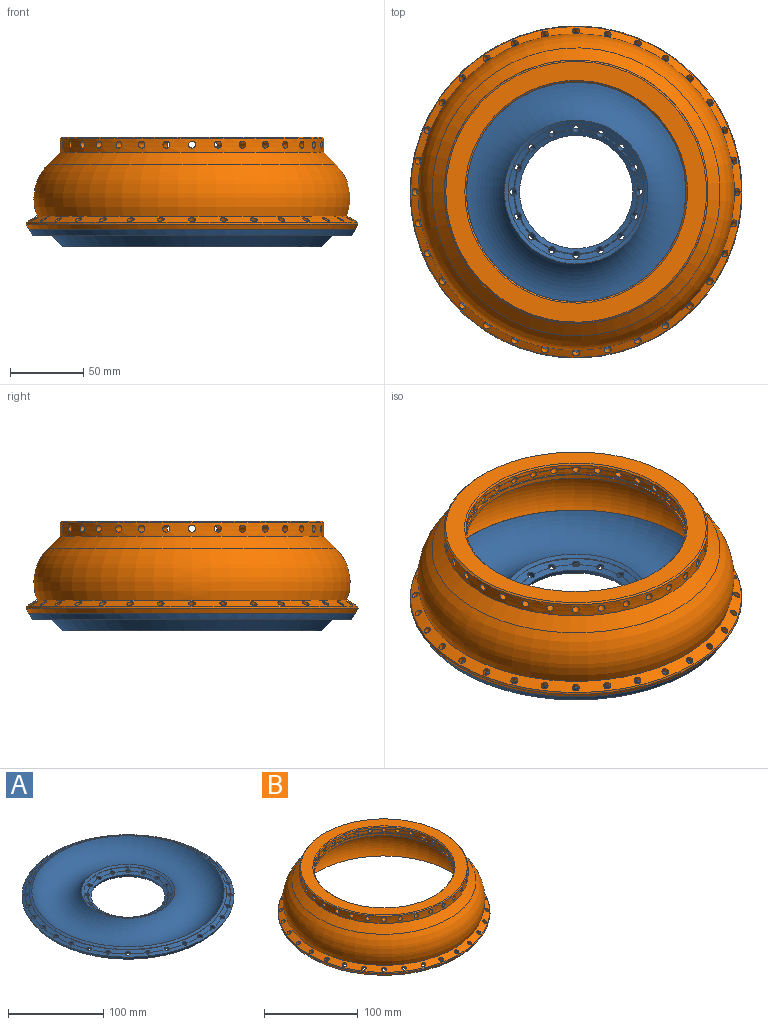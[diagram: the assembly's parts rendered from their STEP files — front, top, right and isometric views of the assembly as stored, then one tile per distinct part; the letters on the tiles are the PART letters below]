
ASSEMBLY  parts=2 mates=1
PART A: 112 faces, bbox 227.3x227.3x33 mm
  f0: cone r=42.59mm half-angle=30deg, axis (0,0,-1), area 12.1mm2, adj f1,f59,f65,f111
  f1: cone r=46.92mm half-angle=60deg, axis (0,0,1), area 1208mm2, adj f0,f2,f3,f4,f5,f6,f7,f8
  f2: cone r=42.59mm half-angle=30deg, axis (0,0,-1), area 12.1mm2, adj f1,f59,f110,f111
  f3: cone r=42.59mm half-angle=30deg, axis (0,0,-1), area 12.1mm2, adj f1,f59,f109,f110
  f4: cone r=42.59mm half-angle=30deg, axis (0,0,-1), area 12.1mm2, adj f1,f59,f108,f109
  f5: cone r=42.59mm half-angle=30deg, axis (0,0,-1), area 12.1mm2, adj f1,f59,f107,f108
  f6: cone r=42.59mm half-angle=30deg, axis (0,0,-1), area 12.1mm2, adj f1,f59,f106,f107
  f7: cone r=42.59mm half-angle=30deg, axis (0,0,-1), area 12.1mm2, adj f1,f59,f105,f106
  f8: cone r=42.59mm half-angle=30deg, axis (0,0,-1), area 12.1mm2, adj f1,f59,f104,f105
  f9: cone r=42.59mm half-angle=30deg, axis (0,0,-1), area 12.1mm2, adj f1,f59,f103,f104
  f10: cone r=42.59mm half-angle=30deg, axis (0,0,-1), area 12.1mm2, adj f1,f59,f102,f103
  f11: cone r=42.59mm half-angle=30deg, axis (0,0,-1), area 12.1mm2, adj f1,f59,f101,f102
  f12: cone r=42.59mm half-angle=30deg, axis (0,0,-1), area 12.1mm2, adj f1,f59,f100,f101
  f13: cone r=42.59mm half-angle=30deg, axis (0,0,-1), area 12.1mm2, adj f1,f59,f99,f100
  f14: cone r=42.59mm half-angle=30deg, axis (0,0,-1), area 12.1mm2, adj f1,f59,f98,f99
  f15: cone r=42.59mm half-angle=30deg, axis (0,0,-1), area 12.1mm2, adj f1,f59,f97,f98
  f16: cone r=107.41mm half-angle=30deg, axis (0,0,1), area 16.5mm2, adj f49,f51,f64,f96
  f17: cone r=107.41mm half-angle=30deg, axis (0,0,1), area 16.5mm2, adj f49,f51,f95,f96
  f18: cone r=107.41mm half-angle=30deg, axis (0,0,1), area 16.5mm2, adj f49,f51,f94,f95
  f19: cone r=107.41mm half-angle=30deg, axis (0,0,1), area 16.5mm2, adj f49,f51,f93,f94
  f20: cone r=107.41mm half-angle=30deg, axis (0,0,1), area 16.5mm2, adj f49,f51,f92,f93
  f21: cone r=107.41mm half-angle=30deg, axis (0,0,1), area 16.5mm2, adj f49,f51,f91,f92
  f22: cone r=107.41mm half-angle=30deg, axis (0,0,1), area 16.5mm2, adj f49,f51,f90,f91
  f23: cone r=107.41mm half-angle=30deg, axis (0,0,1), area 16.5mm2, adj f49,f51,f89,f90
  f24: cone r=107.41mm half-angle=30deg, axis (0,0,1), area 16.5mm2, adj f49,f51,f88,f89
  f25: cone r=107.41mm half-angle=30deg, axis (0,0,1), area 16.5mm2, adj f49,f51,f87,f88
  f26: cone r=107.41mm half-angle=30deg, axis (0,0,1), area 16.5mm2, adj f49,f51,f86,f87
  f27: cone r=107.41mm half-angle=30deg, axis (0,0,1), area 16.5mm2, adj f49,f51,f85,f86
  f28: cone r=107.41mm half-angle=30deg, axis (0,0,1), area 16.5mm2, adj f49,f51,f84,f85
  f29: cone r=107.41mm half-angle=30deg, axis (0,0,1), area 16.5mm2, adj f49,f51,f83,f84
  f30: cone r=107.41mm half-angle=30deg, axis (0,0,1), area 16.5mm2, adj f49,f51,f82,f83
  f31: cone r=107.41mm half-angle=30deg, axis (0,0,1), area 16.5mm2, adj f49,f51,f81,f82
  f32: cone r=107.41mm half-angle=30deg, axis (0,0,1), area 16.5mm2, adj f49,f51,f80,f81
  f33: cone r=107.41mm half-angle=30deg, axis (0,0,1), area 16.5mm2, adj f49,f51,f79,f80
  f34: cone r=107.41mm half-angle=30deg, axis (0,0,1), area 16.5mm2, adj f49,f51,f78,f79
  f35: cone r=107.41mm half-angle=30deg, axis (0,0,1), area 16.5mm2, adj f49,f51,f77,f78
  f36: cone r=107.41mm half-angle=30deg, axis (0,0,1), area 16.5mm2, adj f49,f51,f76,f77
  f37: cone r=107.41mm half-angle=30deg, axis (0,0,1), area 16.5mm2, adj f49,f51,f75,f76
  f38: cone r=107.41mm half-angle=30deg, axis (0,0,1), area 16.5mm2, adj f49,f51,f74,f75
  f39: cone r=107.41mm half-angle=30deg, axis (0,0,1), area 16.5mm2, adj f49,f51,f73,f74
  f40: cone r=107.41mm half-angle=30deg, axis (0,0,1), area 16.5mm2, adj f49,f51,f72,f73
  f41: cone r=107.41mm half-angle=30deg, axis (0,0,1), area 16.5mm2, adj f49,f51,f71,f72
  f42: cone r=107.41mm half-angle=30deg, axis (0,0,1), area 16.5mm2, adj f49,f51,f70,f71
  f43: cone r=107.41mm half-angle=30deg, axis (0,0,1), area 16.5mm2, adj f49,f51,f69,f70
  f44: cone r=107.41mm half-angle=30deg, axis (0,0,1), area 16.5mm2, adj f49,f51,f68,f69
  f45: cone r=107.41mm half-angle=30deg, axis (0,0,1), area 16.5mm2, adj f49,f51,f67,f68
  f46: cone r=107.41mm half-angle=30deg, axis (0,0,1), area 16.5mm2, adj f49,f51,f66,f67
  f47: cone r=100.98mm half-angle=60deg, axis (0,0,-1), area 1927.9mm2, adj f48,f63
  f48: cone r=103.58mm half-angle=30deg, axis (0,0,1), area 649.2mm2, adj f47,f49
  f49: cone r=103.08mm half-angle=60deg, axis (0,0,-1), area 2913.7mm2, adj f16,f17,f18,f19,f20,f21,f22,f23
  f50: cone r=107.41mm half-angle=30deg, axis (0,0,1), area 16.5mm2, adj f49,f51,f64,f66
  f51: cone r=107.91mm half-angle=60deg, axis (0,0,-1), area 2569.7mm2, adj f16,f17,f18,f19,f20,f21,f22,f23
  f52: cone r=111.37mm half-angle=30deg, axis (0,0,1), area 3459.6mm2, adj f51,f53
  f53: cone r=108.87mm half-angle=60deg, axis (0,0,-1), area 5598.7mm2, adj f52,f54,f64,f66,f67,f68,f69,f70
  f54: cone r=100.75mm half-angle=45deg, axis (0,0,1), area 10386.6mm2, adj f53,f55
  f55: plane 176.78x176.78mm, normal (0,0,-1), area 12618.4mm2, adj f54,f56
  f56: cone r=49.25mm half-angle=45deg, axis (0,0,-1), area 6088.1mm2, adj f55,f57
  f57: cone r=41.13mm half-angle=60deg, axis (0,0,1), area 2373.1mm2, adj f56,f58,f65,f97,f98,f99,f100,f101
  f58: cone r=38.63mm half-angle=30deg, axis (0,0,-1), area 1252.8mm2, adj f57,f59
  f59: cone r=42.09mm half-angle=60deg, axis (0,0,1), area 923.1mm2, adj f0,f2,f3,f4,f5,f6,f7,f8
  f60: cone r=42.59mm half-angle=30deg, axis (0,0,-1), area 12.1mm2, adj f1,f59,f65,f97
  f61: cone r=46.42mm half-angle=30deg, axis (0,0,-1), area 293.2mm2, adj f1,f62
  f62: cone r=49.02mm half-angle=60deg, axis (0,0,1), area 899.5mm2, adj f61,f63
  f63: torus R=75mm, axis (0,0,1), area 29608.8mm2, adj f47,f62
  f64: cylinder r=2.4mm len=6.73mm, axis (0.5,0,-0.87), area 66.4mm2, adj f16,f49,f50,f51,f53
  f65: cylinder r=2.4mm len=6.76mm, axis (-0.5,0,-0.87), area 66.4mm2, adj f0,f1,f57,f59,f60
  f66: cylinder r=2.4mm len=6.73mm, axis (0.49,0.1,-0.87), area 66.4mm2, adj f46,f49,f50,f51,f53
  f67: cylinder r=2.4mm len=6.73mm, axis (0.46,0.19,-0.87), area 66.4mm2, adj f45,f46,f49,f51,f53
  f68: cylinder r=2.4mm len=6.73mm, axis (0.42,0.28,-0.87), area 66.4mm2, adj f44,f45,f49,f51,f53
  f69: cylinder r=2.4mm len=6.73mm, axis (0.35,0.35,-0.87), area 66.4mm2, adj f43,f44,f49,f51,f53
  f70: cylinder r=2.4mm len=6.73mm, axis (0.28,0.42,-0.87), area 66.4mm2, adj f42,f43,f49,f51,f53
  f71: cylinder r=2.4mm len=6.73mm, axis (0.19,0.46,-0.87), area 66.4mm2, adj f41,f42,f49,f51,f53
  f72: cylinder r=2.4mm len=6.73mm, axis (0.1,0.49,-0.87), area 66.5mm2, adj f40,f41,f49,f51,f53
  f73: cylinder r=2.4mm len=6.73mm, axis (0,0.5,-0.87), area 66.4mm2, adj f39,f40,f49,f51,f53
  f74: cylinder r=2.4mm len=6.73mm, axis (-0.1,0.49,-0.87), area 66.5mm2, adj f38,f39,f49,f51,f53
  f75: cylinder r=2.4mm len=6.73mm, axis (-0.19,0.46,-0.87), area 66.5mm2, adj f37,f38,f49,f51,f53
  f76: cylinder r=2.4mm len=6.73mm, axis (-0.28,0.42,-0.87), area 66.5mm2, adj f36,f37,f49,f51,f53
  f77: cylinder r=2.4mm len=6.73mm, axis (-0.35,0.35,-0.87), area 66.5mm2, adj f35,f36,f49,f51,f53
  f78: cylinder r=2.4mm len=6.73mm, axis (-0.42,0.28,-0.87), area 66.5mm2, adj f34,f35,f49,f51,f53
  f79: cylinder r=2.4mm len=6.73mm, axis (-0.46,0.19,-0.87), area 66.5mm2, adj f33,f34,f49,f51,f53
  f80: cylinder r=2.4mm len=6.73mm, axis (-0.49,0.1,-0.87), area 66.5mm2, adj f32,f33,f49,f51,f53
  f81: cylinder r=2.4mm len=6.72mm, axis (-0.5,0,-0.87), area 66.4mm2, adj f31,f32,f49,f51,f53
  f82: cylinder r=2.4mm len=6.72mm, axis (-0.49,-0.1,-0.87), area 66.4mm2, adj f30,f31,f49,f51,f53
  f83: cylinder r=2.4mm len=6.72mm, axis (-0.46,-0.19,-0.87), area 66.4mm2, adj f29,f30,f49,f51,f53
  f84: cylinder r=2.4mm len=6.72mm, axis (-0.42,-0.28,-0.87), area 66.4mm2, adj f28,f29,f49,f51,f53
  f85: cylinder r=2.4mm len=6.73mm, axis (-0.35,-0.35,-0.87), area 66.4mm2, adj f27,f28,f49,f51,f53
  f86: cylinder r=2.4mm len=6.73mm, axis (-0.28,-0.42,-0.87), area 66.4mm2, adj f26,f27,f49,f51,f53
  f87: cylinder r=2.4mm len=6.73mm, axis (-0.19,-0.46,-0.87), area 66.4mm2, adj f25,f26,f49,f51,f53
  f88: cylinder r=2.4mm len=6.73mm, axis (-0.1,-0.49,-0.87), area 66.5mm2, adj f24,f25,f49,f51,f53
  f89: cylinder r=2.4mm len=6.73mm, axis (0,-0.5,-0.87), area 66.4mm2, adj f23,f24,f49,f51,f53
  f90: cylinder r=2.4mm len=6.73mm, axis (0.1,-0.49,-0.87), area 66.5mm2, adj f22,f23,f49,f51,f53
  f91: cylinder r=2.4mm len=6.73mm, axis (0.19,-0.46,-0.87), area 66.5mm2, adj f21,f22,f49,f51,f53
  f92: cylinder r=2.4mm len=6.73mm, axis (0.28,-0.42,-0.87), area 66.5mm2, adj f20,f21,f49,f51,f53
  f93: cylinder r=2.4mm len=6.73mm, axis (0.35,-0.35,-0.87), area 66.5mm2, adj f19,f20,f49,f51,f53
  f94: cylinder r=2.4mm len=6.73mm, axis (0.42,-0.28,-0.87), area 66.4mm2, adj f18,f19,f49,f51,f53
  f95: cylinder r=2.4mm len=6.73mm, axis (0.46,-0.19,-0.87), area 66.4mm2, adj f17,f18,f49,f51,f53
  f96: cylinder r=2.4mm len=6.73mm, axis (0.49,-0.1,-0.87), area 66.5mm2, adj f16,f17,f49,f51,f53
  f97: cylinder r=2.4mm len=6.76mm, axis (-0.46,-0.19,-0.87), area 66.4mm2, adj f1,f15,f57,f59,f60
  f98: cylinder r=2.4mm len=6.76mm, axis (-0.35,-0.35,-0.87), area 66.3mm2, adj f1,f14,f15,f57,f59
  f99: cylinder r=2.4mm len=6.76mm, axis (-0.19,-0.46,-0.87), area 66.4mm2, adj f1,f13,f14,f57,f59
  f100: cylinder r=2.4mm len=6.76mm, axis (0,-0.5,-0.87), area 66.4mm2, adj f1,f12,f13,f57,f59
  f101: cylinder r=2.4mm len=6.76mm, axis (0.19,-0.46,-0.87), area 66.4mm2, adj f1,f11,f12,f57,f59
  f102: cylinder r=2.4mm len=6.76mm, axis (0.35,-0.35,-0.87), area 66.4mm2, adj f1,f10,f11,f57,f59
  f103: cylinder r=2.4mm len=6.76mm, axis (0.46,-0.19,-0.87), area 66.4mm2, adj f1,f9,f10,f57,f59
  f104: cylinder r=2.4mm len=6.76mm, axis (0.5,0,-0.87), area 66.3mm2, adj f1,f8,f9,f57,f59
  f105: cylinder r=2.4mm len=6.76mm, axis (0.46,0.19,-0.87), area 66.4mm2, adj f1,f7,f8,f57,f59
  f106: cylinder r=2.4mm len=6.76mm, axis (0.35,0.35,-0.87), area 66.4mm2, adj f1,f6,f7,f57,f59
  f107: cylinder r=2.4mm len=6.76mm, axis (0.19,0.46,-0.87), area 66.4mm2, adj f1,f5,f6,f57,f59
  f108: cylinder r=2.4mm len=6.76mm, axis (0,0.5,-0.87), area 66.4mm2, adj f1,f4,f5,f57,f59
  f109: cylinder r=2.4mm len=6.76mm, axis (-0.19,0.46,-0.87), area 66.4mm2, adj f1,f3,f4,f57,f59
  f110: cylinder r=2.4mm len=6.76mm, axis (-0.35,0.35,-0.87), area 66.4mm2, adj f1,f2,f3,f57,f59
  f111: cylinder r=2.4mm len=6.76mm, axis (-0.46,0.19,-0.87), area 66.3mm2, adj f0,f1,f2,f57,f59
PART B: 157 faces, bbox 233.8x233.8x65.4 mm
  f0: cone r=108.41mm half-angle=30deg, axis (0,0,1), area 16.6mm2, adj f73,f75,f80,f153
  f1: plane 10.45x4.04mm, normal (0,0,-1), area 10.6mm2, adj f64,f66,f150,f152
  f2: cone r=108.41mm half-angle=30deg, axis (0,0,1), area 16.6mm2, adj f73,f75,f149,f151
  f3: plane 9.83x5.88mm, normal (0,0,-1), area 10.6mm2, adj f64,f66,f148,f150
  f4: cone r=108.41mm half-angle=30deg, axis (0,0,1), area 16.6mm2, adj f73,f75,f151,f153
  f5: plane 8.84x7.51mm, normal (0,0,-1), area 10.6mm2, adj f64,f66,f146,f148
  f6: cone r=108.41mm half-angle=30deg, axis (0,0,1), area 16.6mm2, adj f73,f75,f147,f149
  f7: plane 8.84x7.51mm, normal (0,0,-1), area 10.6mm2, adj f64,f66,f144,f146
  f8: cone r=108.41mm half-angle=30deg, axis (0,0,1), area 16.6mm2, adj f73,f75,f145,f147
  f9: plane 9.83x5.88mm, normal (0,0,-1), area 10.6mm2, adj f64,f66,f142,f144
  f10: cone r=108.41mm half-angle=30deg, axis (0,0,1), area 16.6mm2, adj f73,f75,f143,f145
  f11: plane 10.45x4.04mm, normal (0,0,-1), area 10.6mm2, adj f64,f66,f140,f142
  f12: cone r=108.41mm half-angle=30deg, axis (0,0,1), area 16.6mm2, adj f73,f75,f141,f143
  f13: plane 10.67x2.03mm, normal (0,0,-1), area 10.6mm2, adj f64,f66,f138,f140
  f14: cone r=108.41mm half-angle=30deg, axis (0,0,1), area 16.6mm2, adj f73,f75,f139,f141
  f15: plane 10.67x2.03mm, normal (0,0,-1), area 10.6mm2, adj f64,f66,f136,f138
  f16: cone r=108.41mm half-angle=30deg, axis (0,0,1), area 16.6mm2, adj f73,f75,f137,f139
  f17: plane 10.45x4.04mm, normal (0,0,-1), area 10.6mm2, adj f64,f66,f134,f136
  f18: cone r=108.41mm half-angle=30deg, axis (0,0,1), area 16.6mm2, adj f73,f75,f135,f137
  f19: plane 9.83x5.88mm, normal (0,0,-1), area 10.6mm2, adj f64,f66,f132,f134
  f20: cone r=108.41mm half-angle=30deg, axis (0,0,1), area 16.6mm2, adj f73,f75,f133,f135
  f21: plane 8.84x7.51mm, normal (0,0,-1), area 10.6mm2, adj f64,f66,f129,f132
  f22: cone r=108.41mm half-angle=30deg, axis (0,0,1), area 16.6mm2, adj f73,f75,f130,f133
  f23: plane 8.84x7.51mm, normal (0,0,-1), area 10.6mm2, adj f64,f66,f126,f129
  f24: cone r=108.41mm half-angle=30deg, axis (0,0,1), area 16.6mm2, adj f73,f75,f127,f131
  f25: plane 9.83x5.88mm, normal (0,0,-1), area 10.6mm2, adj f64,f66,f123,f126
  f26: cone r=108.41mm half-angle=30deg, axis (0,0,1), area 16.6mm2, adj f73,f75,f124,f128
  f27: plane 10.45x4.04mm, normal (0,0,-1), area 10.6mm2, adj f64,f66,f120,f123
  f28: cone r=108.41mm half-angle=30deg, axis (0,0,1), area 16.6mm2, adj f73,f75,f121,f125
  f29: plane 10.67x2.03mm, normal (0,0,-1), area 10.6mm2, adj f64,f66,f117,f120
  f30: cone r=108.41mm half-angle=30deg, axis (0,0,1), area 16.6mm2, adj f73,f75,f119,f122
  f31: plane 10.67x2.03mm, normal (0,0,-1), area 10.6mm2, adj f64,f66,f114,f117
  f32: cone r=108.41mm half-angle=30deg, axis (0,0,1), area 16.6mm2, adj f73,f75,f116,f118
  f33: plane 10.45x4.04mm, normal (0,0,-1), area 10.6mm2, adj f64,f66,f111,f114
  f34: cone r=108.41mm half-angle=30deg, axis (0,0,1), area 16.6mm2, adj f73,f75,f113,f115
  f35: plane 9.83x5.88mm, normal (0,0,-1), area 10.6mm2, adj f64,f66,f108,f111
  f36: cone r=108.41mm half-angle=30deg, axis (0,0,1), area 16.6mm2, adj f73,f75,f110,f112
  f37: plane 8.84x7.51mm, normal (0,0,-1), area 10.6mm2, adj f64,f66,f105,f108
  f38: cone r=108.41mm half-angle=30deg, axis (0,0,1), area 16.6mm2, adj f73,f75,f106,f109
  f39: plane 8.84x7.51mm, normal (0,0,-1), area 10.6mm2, adj f64,f66,f103,f105
  f40: cone r=108.41mm half-angle=30deg, axis (0,0,1), area 16.6mm2, adj f73,f75,f104,f107
  f41: plane 9.83x5.88mm, normal (0,0,-1), area 10.6mm2, adj f64,f66,f100,f103
  f42: cone r=108.41mm half-angle=30deg, axis (0,0,1), area 16.6mm2, adj f73,f75,f101,f104
  f43: plane 10.45x4.04mm, normal (0,0,-1), area 10.6mm2, adj f64,f66,f98,f100
  f44: cone r=108.41mm half-angle=30deg, axis (0,0,1), area 16.6mm2, adj f73,f75,f99,f102
  f45: plane 10.67x2.03mm, normal (0,0,-1), area 10.6mm2, adj f64,f66,f96,f98
  f46: cone r=108.41mm half-angle=30deg, axis (0,0,1), area 16.6mm2, adj f73,f75,f97,f99
  f47: plane 10.67x2.03mm, normal (0,0,-1), area 10.6mm2, adj f64,f66,f94,f96
  f48: cone r=108.41mm half-angle=30deg, axis (0,0,1), area 16.6mm2, adj f73,f75,f95,f97
  f49: plane 10.45x4.04mm, normal (0,0,-1), area 10.6mm2, adj f64,f66,f92,f94
  f50: cone r=108.41mm half-angle=30deg, axis (0,0,1), area 16.6mm2, adj f73,f75,f93,f95
  f51: plane 9.83x5.88mm, normal (0,0,-1), area 10.6mm2, adj f64,f66,f89,f92
  f52: cone r=108.41mm half-angle=30deg, axis (0,0,1), area 16.6mm2, adj f73,f75,f91,f93
  f53: plane 8.84x7.51mm, normal (0,0,-1), area 10.6mm2, adj f64,f66,f87,f89
  f54: cone r=108.41mm half-angle=30deg, axis (0,0,1), area 16.6mm2, adj f73,f75,f88,f90
  f55: plane 8.84x7.51mm, normal (0,0,-1), area 10.6mm2, adj f64,f66,f85,f87
  f56: cone r=108.41mm half-angle=30deg, axis (0,0,1), area 16.6mm2, adj f73,f75,f86,f88
  f57: plane 9.83x5.88mm, normal (0,0,-1), area 10.6mm2, adj f64,f66,f83,f85
  f58: cone r=108.41mm half-angle=30deg, axis (0,0,1), area 16.6mm2, adj f73,f75,f84,f86
  f59: plane 10.45x4.04mm, normal (0,0,-1), area 10.6mm2, adj f64,f66,f81,f83
  f60: cone r=108.41mm half-angle=30deg, axis (0,0,1), area 16.6mm2, adj f73,f75,f82,f84
  f61: plane 10.67x2.03mm, normal (0,0,-1), area 10.6mm2, adj f64,f66,f79,f81
  f62: cylinder r=75mm len=150mm, axis (0,0,-1), area 1413.7mm2, adj f63,f78
  f63: plane 152x152mm, normal (0,0,1), area 474.4mm2, adj f62,f64
  f64: cylinder r=76mm len=152mm, axis (0,0,-1), area 1923.7mm2, adj f1,f3,f5,f7,f9,f11,f13,f15
  f65: plane 10.67x2.03mm, normal (0,0,-1), area 10.6mm2, adj f64,f66,f79,f152
  f66: cylinder r=75mm len=150mm, axis (0,0,-1), area 1295.9mm2, adj f1,f3,f5,f7,f9,f11,f13,f15
  f67: plane 178x178mm, normal (0,0,1), area 6738.7mm2, adj f155,f156
  f68: cylinder r=90mm len=180mm, axis (0,0,-1), area 4707.4mm2, adj f69,f79,f81,f83,f85,f87,f89,f92
  f69: cone r=98.33mm half-angle=45deg, axis (0,0,-1), area 6973.9mm2, adj f68,f70
  f70: torus R=75mm, axis (0,0,-1), area 25312.9mm2, adj f69,f71
  f71: cone r=113.87mm half-angle=60deg, axis (0,0,-1), area 5179.1mm2, adj f70,f80,f82,f84,f86,f88,f90,f93
  f72: cone r=111.37mm half-angle=30deg, axis (0,0,1), area 2824.2mm2, adj f73,f154
  f73: cone r=107.91mm half-angle=60deg, axis (0,0,-1), area 2569.5mm2, adj f0,f2,f4,f6,f8,f10,f12,f14
  f74: cone r=108.41mm half-angle=30deg, axis (0,0,1), area 16.6mm2, adj f73,f75,f80,f82
  f75: cone r=104.08mm half-angle=60deg, axis (0,0,-1), area 2943.9mm2, adj f0,f2,f4,f6,f8,f10,f12,f14
  f76: cone r=103.58mm half-angle=30deg, axis (0,0,1), area 652.4mm2, adj f75,f77
  f77: cone r=100.98mm half-angle=60deg, axis (0,0,-1), area 1927.9mm2, adj f76,f78
  f78: torus R=75mm, axis (0,0,-1), area 38091.1mm2, adj f62,f77
  f79: cylinder r=2.4mm len=15.03mm, axis (-1,0,0), area 216.3mm2, adj f61,f64,f65,f66,f68
  f80: cylinder r=2.4mm len=6.74mm, axis (-0.5,0,0.87), area 66.6mm2, adj f0,f71,f73,f74,f75
  f81: cylinder r=2.4mm len=15.68mm, axis (-0.98,-0.2,0), area 216.3mm2, adj f59,f61,f64,f66,f68
  f82: cylinder r=2.4mm len=6.74mm, axis (-0.49,-0.1,0.87), area 66.6mm2, adj f60,f71,f73,f74,f75
  f83: cylinder r=2.4mm len=15.72mm, axis (-0.92,-0.38,0), area 216.3mm2, adj f57,f59,f64,f66,f68
  f84: cylinder r=2.4mm len=6.74mm, axis (-0.46,-0.19,0.87), area 66.6mm2, adj f58,f60,f71,f73,f75
  f85: cylinder r=2.4mm len=15.16mm, axis (-0.83,-0.56,0), area 216.3mm2, adj f55,f57,f64,f66,f68
  f86: cylinder r=2.4mm len=6.74mm, axis (-0.42,-0.28,0.87), area 66.6mm2, adj f56,f58,f71,f73,f75
  f87: cylinder r=2.4mm len=14.02mm, axis (-0.71,-0.71,0), area 216.3mm2, adj f53,f55,f64,f66,f68
  f88: cylinder r=2.4mm len=6.74mm, axis (-0.35,-0.35,0.87), area 66.6mm2, adj f54,f56,f71,f73,f75
  f89: cylinder r=2.4mm len=15.16mm, axis (-0.56,-0.83,0), area 216.3mm2, adj f51,f53,f64,f66,f68
  f90: cylinder r=2.4mm len=6.74mm, axis (-0.28,-0.42,0.87), area 66.6mm2, adj f54,f71,f73,f75,f91
  f91: cylinder r=2.4mm len=0.87mm, axis (-0.28,-0.42,0.87), area 0mm2, adj f52,f73,f90
  f92: cylinder r=2.4mm len=15.72mm, axis (-0.38,-0.92,0), area 216.3mm2, adj f49,f51,f64,f66,f68
  f93: cylinder r=2.4mm len=6.74mm, axis (-0.19,-0.46,0.87), area 66.6mm2, adj f50,f52,f71,f73,f75
  f94: cylinder r=2.4mm len=15.68mm, axis (-0.2,-0.98,0), area 216.3mm2, adj f47,f49,f64,f66,f68
  f95: cylinder r=2.4mm len=6.74mm, axis (-0.1,-0.49,0.87), area 66.6mm2, adj f48,f50,f71,f73,f75
  f96: cylinder r=2.4mm len=15.03mm, axis (0,-1,0), area 216.3mm2, adj f45,f47,f64,f66,f68
  f97: cylinder r=2.4mm len=6.73mm, axis (0,-0.5,0.87), area 66.6mm2, adj f46,f48,f71,f73,f75
  f98: cylinder r=2.4mm len=15.68mm, axis (0.2,-0.98,0), area 216.3mm2, adj f43,f45,f64,f66,f68
  f99: cylinder r=2.4mm len=6.73mm, axis (0.1,-0.49,0.87), area 66.5mm2, adj f44,f46,f71,f73,f75
  f100: cylinder r=2.4mm len=15.72mm, axis (0.38,-0.92,0), area 216.3mm2, adj f41,f43,f64,f66,f68
  f101: cylinder r=2.4mm len=6.73mm, axis (0.19,-0.46,0.87), area 66.5mm2, adj f42,f71,f73,f75,f102
  f102: cylinder r=2.4mm len=0.87mm, axis (0.19,-0.46,0.87), area 0mm2, adj f44,f73,f101
  f103: cylinder r=2.4mm len=15.16mm, axis (0.56,-0.83,0), area 216.3mm2, adj f39,f41,f64,f66,f68
  f104: cylinder r=2.4mm len=6.73mm, axis (0.28,-0.42,0.87), area 66.5mm2, adj f40,f42,f71,f73,f75
  f105: cylinder r=2.4mm len=14.02mm, axis (0.71,-0.71,0), area 216.3mm2, adj f37,f39,f64,f66,f68
  f106: cylinder r=2.4mm len=6.74mm, axis (0.35,-0.35,0.87), area 66.5mm2, adj f38,f71,f73,f75,f107
  f107: cylinder r=2.4mm len=0.87mm, axis (0.35,-0.35,0.87), area 0mm2, adj f40,f73,f106
  f108: cylinder r=2.4mm len=15.16mm, axis (0.83,-0.56,0), area 216.3mm2, adj f35,f37,f64,f66,f68
  f109: cylinder r=2.4mm len=6.73mm, axis (0.42,-0.28,0.87), area 66.5mm2, adj f38,f71,f73,f75,f110
  f110: cylinder r=2.4mm len=0.87mm, axis (0.42,-0.28,0.87), area 0mm2, adj f36,f73,f109
  f111: cylinder r=2.4mm len=15.72mm, axis (0.92,-0.38,0), area 216.3mm2, adj f33,f35,f64,f66,f68
  f112: cylinder r=2.4mm len=6.73mm, axis (0.46,-0.19,0.87), area 66.5mm2, adj f36,f71,f73,f75,f113
  f113: cylinder r=2.4mm len=0.87mm, axis (0.46,-0.19,0.87), area 0mm2, adj f34,f73,f112
  f114: cylinder r=2.4mm len=15.68mm, axis (0.98,-0.2,0), area 216.3mm2, adj f31,f33,f64,f66,f68
  f115: cylinder r=2.4mm len=6.74mm, axis (0.49,-0.1,0.87), area 66.6mm2, adj f34,f71,f73,f75,f116
  f116: cylinder r=2.4mm len=0.87mm, axis (0.49,-0.1,0.87), area 0mm2, adj f32,f73,f115
  f117: cylinder r=2.4mm len=15.03mm, axis (1,0,0), area 216.3mm2, adj f29,f31,f64,f66,f68
  f118: cylinder r=2.4mm len=6.74mm, axis (0.5,0,0.87), area 66.6mm2, adj f32,f71,f73,f75,f119
  f119: cylinder r=2.4mm len=0.87mm, axis (0.5,0,0.87), area 0mm2, adj f30,f73,f118
  f120: cylinder r=2.4mm len=15.68mm, axis (0.98,0.2,0), area 216.3mm2, adj f27,f29,f64,f66,f68
  f121: cylinder r=2.4mm len=6.74mm, axis (0.49,0.1,0.87), area 66.6mm2, adj f28,f71,f73,f75,f122
  f122: cylinder r=2.4mm len=0.87mm, axis (0.49,0.1,0.87), area 0mm2, adj f30,f73,f121
  f123: cylinder r=2.4mm len=15.72mm, axis (0.92,0.38,0), area 216.3mm2, adj f25,f27,f64,f66,f68
  f124: cylinder r=2.4mm len=6.73mm, axis (0.46,0.19,0.87), area 66.5mm2, adj f26,f71,f73,f75,f125
  f125: cylinder r=2.4mm len=0.87mm, axis (0.46,0.19,0.87), area 0mm2, adj f28,f73,f124
  f126: cylinder r=2.4mm len=15.16mm, axis (0.83,0.56,0), area 216.3mm2, adj f23,f25,f64,f66,f68
  f127: cylinder r=2.4mm len=6.74mm, axis (0.42,0.28,0.87), area 66.6mm2, adj f24,f71,f73,f75,f128
  f128: cylinder r=2.4mm len=0.87mm, axis (0.42,0.28,0.87), area 0mm2, adj f26,f73,f127
  f129: cylinder r=2.4mm len=14.02mm, axis (0.71,0.71,0), area 216.3mm2, adj f21,f23,f64,f66,f68
  f130: cylinder r=2.4mm len=6.74mm, axis (0.35,0.35,0.87), area 66.6mm2, adj f22,f71,f73,f75,f131
  f131: cylinder r=2.4mm len=0.87mm, axis (0.35,0.35,0.87), area 0mm2, adj f24,f73,f130
  f132: cylinder r=2.4mm len=15.16mm, axis (0.56,0.83,0), area 216.3mm2, adj f19,f21,f64,f66,f68
  f133: cylinder r=2.4mm len=6.74mm, axis (0.28,0.42,0.87), area 66.6mm2, adj f20,f22,f71,f73,f75
  f134: cylinder r=2.4mm len=15.72mm, axis (0.38,0.92,0), area 216.3mm2, adj f17,f19,f64,f66,f68
  f135: cylinder r=2.4mm len=6.73mm, axis (0.19,0.46,0.87), area 66.5mm2, adj f18,f20,f71,f73,f75
  f136: cylinder r=2.4mm len=15.68mm, axis (0.2,0.98,0), area 216.3mm2, adj f15,f17,f64,f66,f68
  f137: cylinder r=2.4mm len=6.74mm, axis (0.1,0.49,0.87), area 66.6mm2, adj f16,f18,f71,f73,f75
  f138: cylinder r=2.4mm len=15.03mm, axis (0,1,0), area 216.3mm2, adj f13,f15,f64,f66,f68
  f139: cylinder r=2.4mm len=6.74mm, axis (0,0.5,0.87), area 66.6mm2, adj f14,f16,f71,f73,f75
  f140: cylinder r=2.4mm len=15.68mm, axis (-0.2,0.98,0), area 216.3mm2, adj f11,f13,f64,f66,f68
  f141: cylinder r=2.4mm len=6.74mm, axis (-0.1,0.49,0.87), area 66.6mm2, adj f12,f14,f71,f73,f75
  f142: cylinder r=2.4mm len=15.72mm, axis (-0.38,0.92,0), area 216.3mm2, adj f9,f11,f64,f66,f68
  f143: cylinder r=2.4mm len=6.73mm, axis (-0.19,0.46,0.87), area 66.6mm2, adj f10,f12,f71,f73,f75
  f144: cylinder r=2.4mm len=15.16mm, axis (-0.56,0.83,0), area 216.3mm2, adj f7,f9,f64,f66,f68
  f145: cylinder r=2.4mm len=6.73mm, axis (-0.28,0.42,0.87), area 66.5mm2, adj f8,f10,f71,f73,f75
  f146: cylinder r=2.4mm len=14.02mm, axis (-0.71,0.71,0), area 216.3mm2, adj f5,f7,f64,f66,f68
  f147: cylinder r=2.4mm len=6.73mm, axis (-0.35,0.35,0.87), area 66.5mm2, adj f6,f8,f71,f73,f75
  f148: cylinder r=2.4mm len=15.16mm, axis (-0.83,0.56,0), area 216.3mm2, adj f3,f5,f64,f66,f68
  f149: cylinder r=2.4mm len=6.73mm, axis (-0.42,0.28,0.87), area 66.5mm2, adj f2,f6,f71,f73,f75
  f150: cylinder r=2.4mm len=15.72mm, axis (-0.92,0.38,0), area 216.3mm2, adj f1,f3,f64,f66,f68
  f151: cylinder r=2.4mm len=6.73mm, axis (-0.46,0.19,0.87), area 66.5mm2, adj f2,f4,f71,f73,f75
  f152: cylinder r=2.4mm len=15.68mm, axis (-0.98,0.2,0), area 216.3mm2, adj f1,f64,f65,f66,f68
  f153: cylinder r=2.4mm len=6.73mm, axis (-0.49,0.1,0.87), area 66.5mm2, adj f0,f4,f71,f73,f75
  f154: cone r=113.37mm half-angle=15deg, axis (0,0,-1), area 1005.8mm2, adj f71,f72
  f155: cone r=76mm half-angle=45deg, axis (0,0,1), area 670.9mm2, adj f66,f67
  f156: cone r=90mm half-angle=45deg, axis (0,0,-1), area 795.3mm2, adj f67,f68
PLACE A t=(32.47,35.28,14.3)mm
PLACE B t=(32.47,35.28,14.3)mm
MATE fastened A.f0 <-> B.f0  axis (0,0,-1) through (32.47,35.28,-1.45)mm
